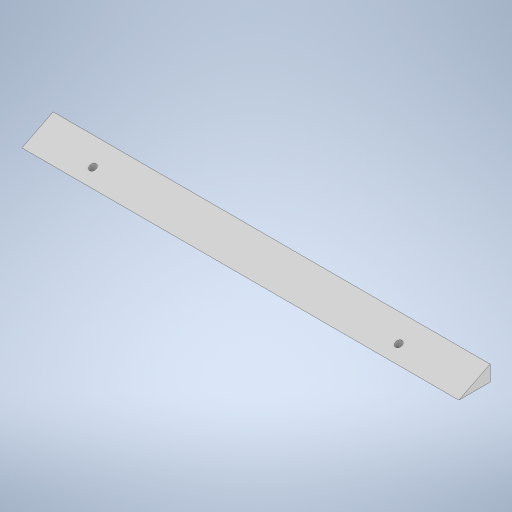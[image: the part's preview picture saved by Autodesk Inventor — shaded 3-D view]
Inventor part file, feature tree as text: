
AUTODESK INVENTOR PART (.ipt)
format: ipt  version: 2023 (Build 270158000, 158)  size: 248,320 bytes
history: native  units: in
note: dims shown in document units (in); Inventor stores cm internally (conversion verified against a paired STEP export)
features: sketch x3, extrude x2, hole x1
ambient origin geometry x8: Origin, YZ Plane, XZ Plane, XY Plane, X Axis, Y Axis, Z Axis, Center Point
bodies: Solid1 (feature_tree)
feature tree (6):
  extrude  "Extrusion1"  Depth=0.3937in
  extrude  "Extrusion3"  Depth=0.7874in TaperAngle=0.0deg
  hole  "Hole1"  [1 undecoded]
  sketch  "Sketch1"  dims[d0=11.0236in d1=0.3937in]
  sketch  "Sketch3"  dims[d2=0.7874in d3=0.0in d6=0.7874in d7=0.0in]
  sketch  "Sketch5"  dims[d8=0.1575in d9=0.1575in d10=7.7165in d11=0.315in d12=0.315in d13=1.4764in d14=0.1575in d15=0.315in d16=0.1575in d17=0.0787in d18=90.0deg d19=0.1969in d20=0.8108in]
note: 1 required parameter value undecoded (feature->parameter linkage not recoverable at this tier; creation-order binding heuristic only, values carry confidence <= 0.55)
